# Revit family: NLRS_57_DUA_UN_Firedamper_LT_BDFC_Solid_Air
name_source: partatom
category: Duct Accessories
revit_build: Autodesk Revit 2017 (Build: 20190508_0315(x64)
units: mm (PartAtom-declared; Revit-internal decimal feet)

## family parameters
Always vertical = No
Cut with Voids When Loaded = No
Part Type = Breaks Into
Round Connector Dimension = Use Diameter
Shared = No
Work Plane-Based = No

## types (1)
- BFDC
    Article_Codes = BFDC_Article_Codes
    Article_Data = BFDC_Article_Data
    Assembly Code = 57.70
    Blade material = Promatect
    Casing material = Galvanized Steel
    Description = Ronde brandklep
    FireRating = EN 1366-2 and EN 13501-3, 2h
    Fuse temperatuur (default) = 72 degrees Celsius
    IfcDescription = Ronde brandklep
    IfcExportAs = IfcDamperType
    IfcExportType = FIREDAMPER
    LoadBearing = No
    Manufacturer = Solid Air Climate Solutions
    Model = Brandklep - Rond
    NLRS_C_content_datum_uitgifte = 10-03-2020
    NLRS_C_content_provider = Solid Air Climate Systems
    NLRS_C_content_versie = Versie 1.7
    NLRS_C_description = Ronde brandklep
    NLRS_C_niveau ontwikkeling = LOD400
    SACS_AX_Prefix = 925
    SACS_Dummy = 1
    SACS_Length_X = 66 mm  [stored 0.216535 ft]
    SACS_Length_Y = 5 mm  [stored 0.0164042 ft]
    Show Symbol = Yes
    Type Comments = This damper is installed INSIDE a round duct.
    URL = https://solid-air.nl

note: [stored X ft] marks values corroborated as IEEE doubles in the binary element streams (Revit-internal decimal feet)

## geometry (parser evidence)
native form markers: Sweep x4
no freeform markers — native parametric forms only
